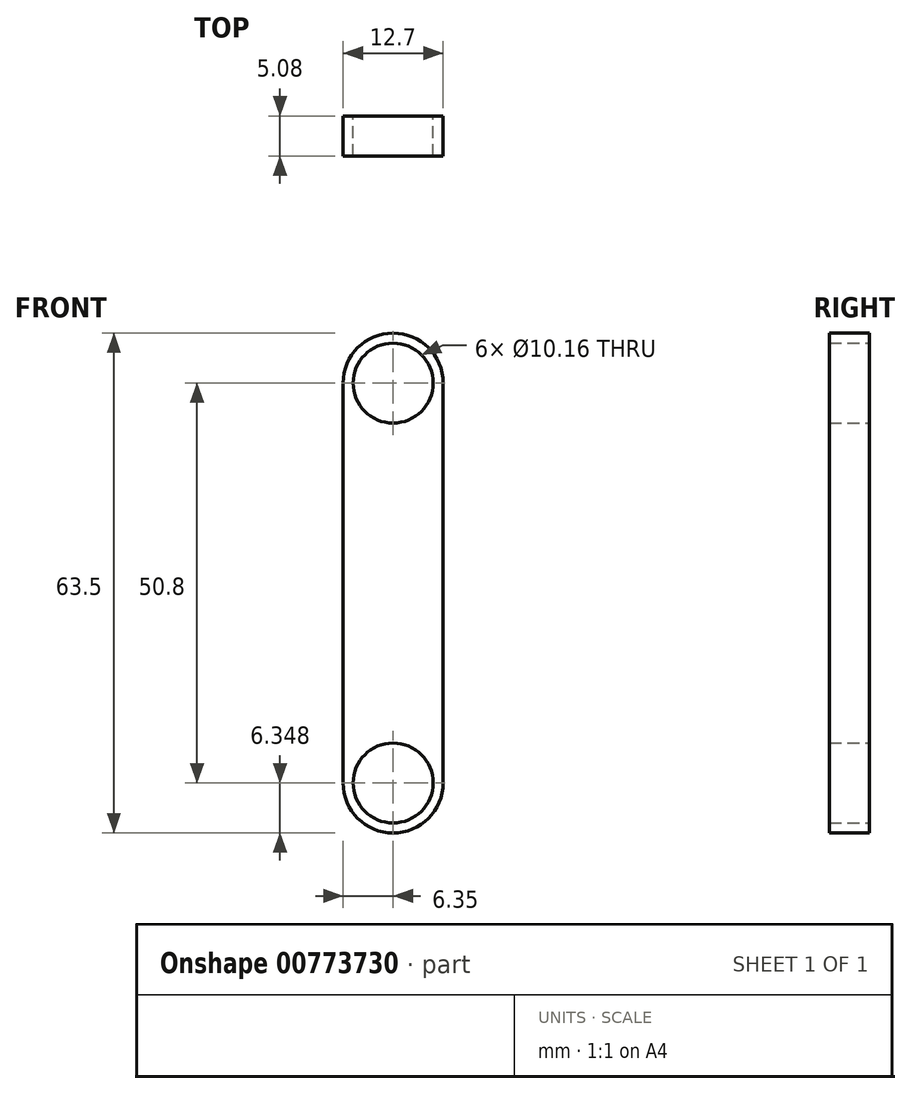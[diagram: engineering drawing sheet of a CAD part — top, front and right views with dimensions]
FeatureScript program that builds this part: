
annotation { "Feature Type Name" : "Feature", "Feature Type Description" : "" }
export const myFeature = defineFeature(function(context is Context, id is Id, definition is map)
    precondition{}
    {
        {
            var Q0;
            Q0=qCreatedBy(makeId("Front.planeOp"),FACE);
            var sketch = newSketch(context, id + "F0", { "sketchPlane" : qUnion([Q0])});
            skCircle(sketch, "E0", {"center": v(0, 23.6) * mm, "radius": 6.35 * mm});
            skCircle(sketch, "E1", {"center": v(0, 23.6) * mm, "radius": 5.08 * mm});
            skCircle(sketch, "E2", {"center": v(0, -27.2) * mm, "radius": 5.08 * mm});
            skCircle(sketch, "E3", {"center": v(0, -27.2) * mm, "radius": 6.35 * mm});
            skLineSegment(sketch, "E4", {"start": v(-6.35, 23.6) * mm, "end": v(-6.35, -27.2) * mm});
            skLineSegment(sketch, "E5", {"start": v(6.35, -27.2) * mm, "end": v(6.35, 23.6) * mm});
            skSolve(sketch);
        }
        {
            var Q0;
            {var subQ0=sQuery(id+"F0.wireOp",EDGE,"E4");Q0=makeQuery(id+"F0.imprint","IMPRINT",FACE,{"disambiguationData":[TD([[makeQuery(id+"F0.imprint","IMPRINT",EDGE,{"derivedFrom":subQ0}),1.0]])]});}
            var Q1;
            Q1=makeQuery(id+"F0.imprint","IMPRINT",FACE,{"disambiguationData":[TD([[makeQuery(id+"F0.imprint","IMPRINT",EDGE,{"derivedFrom":sQuery(id+"F0.wireOp",EDGE,"E1")}),-1.0]])]});
            var Q2;
            Q2=makeQuery(id+"F0.imprint","IMPRINT",FACE,{"disambiguationData":[TD([[makeQuery(id+"F0.imprint","IMPRINT",EDGE,{"derivedFrom":sQuery(id+"F0.wireOp",EDGE,"E2")}),-1.0]])]});
            extrude(context, id + "F1", {"entities" : qUnion([Q0, Q1, Q2]), "depth" : 5.08 * mm, "offsetDistance" : 25.4 * mm});
        }
    });
